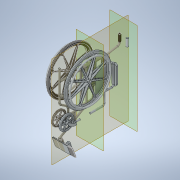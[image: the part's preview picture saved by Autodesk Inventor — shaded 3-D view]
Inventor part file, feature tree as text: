
AUTODESK INVENTOR PART (.ipt)
format: ipt  version: 2021 (Build 250183000, 183)  size: 1,130,496 bytes
history: native  units: mm
features: other x13, plane x2, extrude x2, sketch x2, mirror x1
ambient origin geometry x8: Origin, YZ Plane, XZ Plane, XY Plane, X Axis, Y Axis, Z Axis, Center Point
bodies: Solid1 (feature_tree), Solid2 (feature_tree), Solid5 (feature_tree), Solid7 (feature_tree), Solid10 (feature_tree), Solid11 (feature_tree), Solid13 (feature_tree), Solid17 (feature_tree), Solid18 (feature_tree), Solid19 (feature_tree), Solid20 (feature_tree), Solid24 (feature_tree), Solid26 (feature_tree)
feature tree (20):
  plane  "Work Plane1"
  extrude  "Extrusion1"  Depth=500.0mm TaperAngle=0.0deg
  mirror  "Mirror1"
  plane  "Work Plane2"
  extrude  "Extrusion3"  Depth=10.0mm TaperAngle=0.0deg
  sketch  "Sketch1"  dims[d0=50.0mm d1=500.0mm d2=0.0mm]
  sketch  "Sketch3"  dims[d5=-440.0mm d6=10.0mm d7=0.0mm]
  other  "SideFrame_1:1"
  other  "SideFrame_1:2"
  other  "SideFrame_1:5"
  other  "SideFrame_1:7"
  other  "Arm_3:1"
  other  "Arm_3:2"
  other  "ArmPad_5:1"
  other  "WheelLarge_8:1"
  other  "WheelLarge_8:2"
  other  "WheelSmall_16:1"
  other  "CasterFork_17:1"
  other  "FootRest_12:1"
  other  "Grip_14:1"
